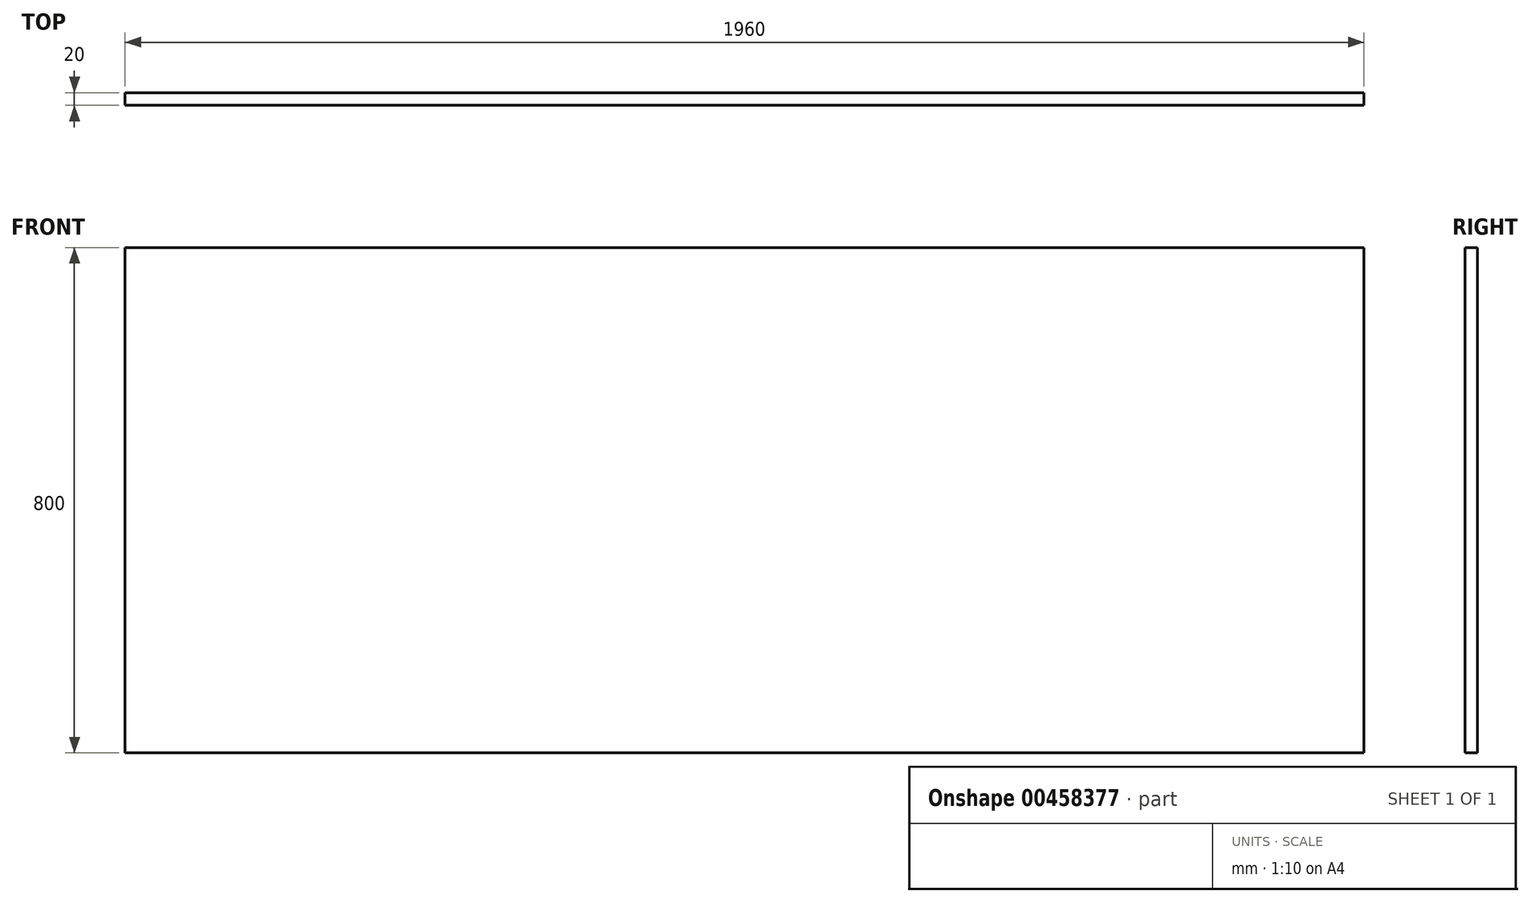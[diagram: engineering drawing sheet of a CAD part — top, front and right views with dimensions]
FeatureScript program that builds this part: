
annotation { "Feature Type Name" : "Feature", "Feature Type Description" : "" }
export const myFeature = defineFeature(function(context is Context, id is Id, definition is map)
    precondition{}
    {
        {
            var Q0;
            Q0=qCreatedBy(makeId("Front.planeOp"),FACE);
            var sketch = newSketch(context, id + "F0", { "sketchPlane" : qUnion([Q0])});
            skLineSegment(sketch, "E0.bottom", {"start": v(-708.6, -356.8) * mm, "end": v(1251.4, -356.8) * mm});
            skLineSegment(sketch, "E0.top", {"start": v(-708.6, 443.2) * mm, "end": v(1251.4, 443.2) * mm});
            skLineSegment(sketch, "E0.left", {"start": v(-708.6, -356.8) * mm, "end": v(-708.6, 443.2) * mm});
            skLineSegment(sketch, "E0.right", {"start": v(1251.4, -356.8) * mm, "end": v(1251.4, 443.2) * mm});
            skSolve(sketch);
        }
        {
            var Q0;
            Q0=makeQuery(id+"F0.imprint","IMPRINT",FACE,{"disambiguationData":[TD([[makeQuery(id+"F0.imprint","IMPRINT",EDGE,{"derivedFrom":sQuery(id+"F0.wireOp",EDGE,"E0.bottom")}),1.0]])]});
            extrude(context, id + "F1", {"entities" : qUnion([Q0]), "depth" : 20 * mm});
        }
    });
